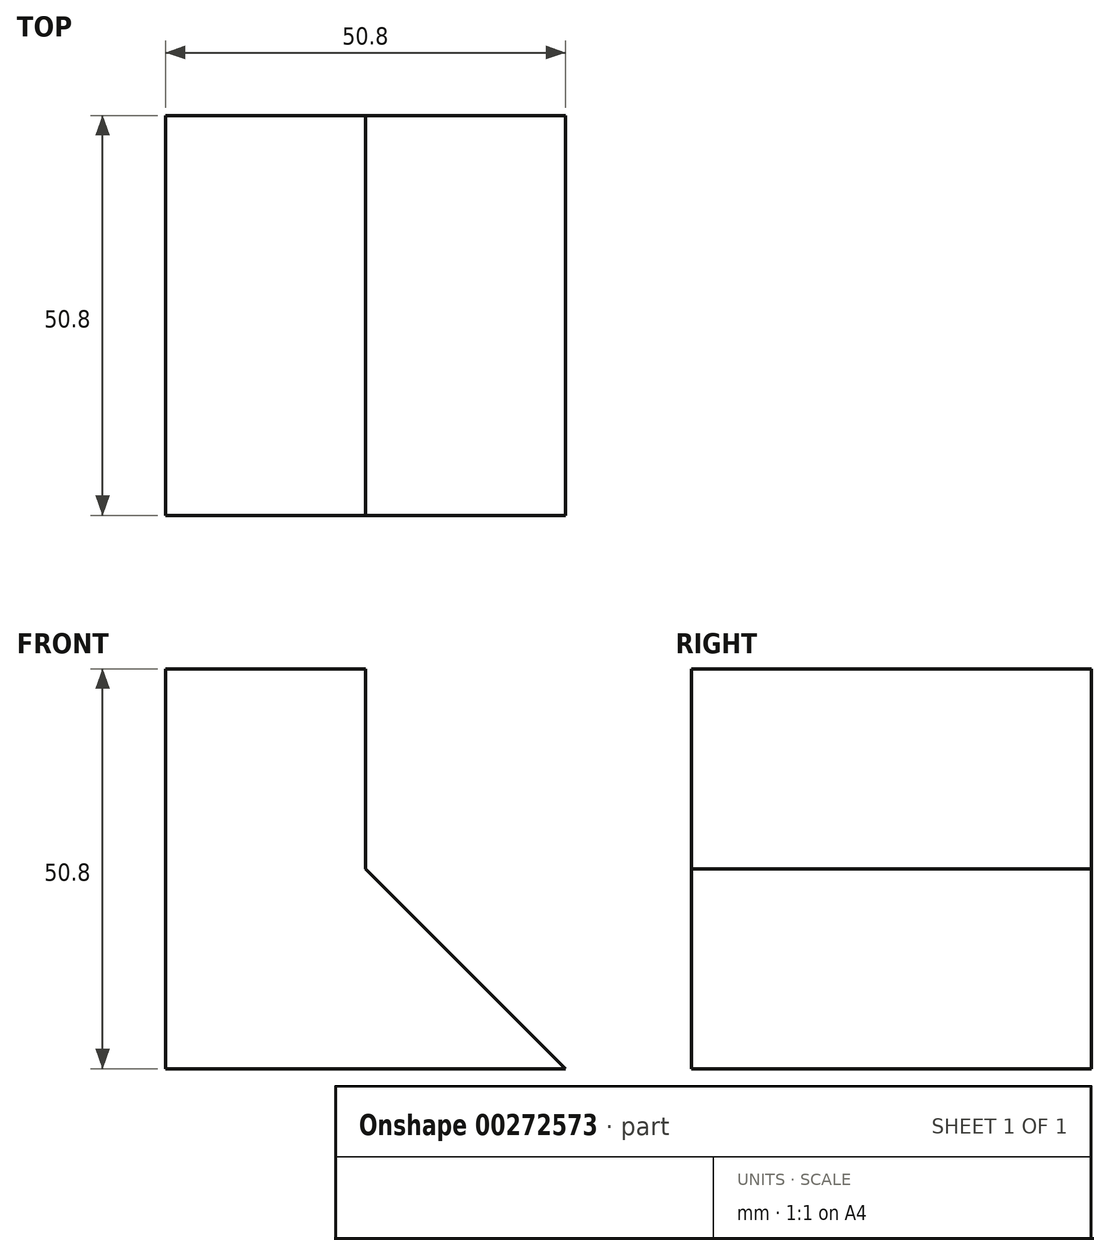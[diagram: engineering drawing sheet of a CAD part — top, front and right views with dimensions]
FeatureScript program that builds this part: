
annotation { "Feature Type Name" : "Feature", "Feature Type Description" : "" }
export const myFeature = defineFeature(function(context is Context, id is Id, definition is map)
    precondition{}
    {
        {
            var Q0;
            Q0=qCreatedBy(makeId("Front.planeOp"),FACE);
            var sketch = newSketch(context, id + "F0", { "sketchPlane" : qUnion([Q0])});
            skLineSegment(sketch, "E0", {"start": v(0, 0) * mm, "end": v(-50.8, 0) * mm});
            skLineSegment(sketch, "E1", {"start": v(-50.8, 0) * mm, "end": v(-50.8, 50.8) * mm});
            skLineSegment(sketch, "E2", {"start": v(-50.8, 50.8) * mm, "end": v(-25.4, 50.8) * mm});
            skLineSegment(sketch, "E3", {"start": v(-25.4, 50.8) * mm, "end": v(-25.4, 25.4) * mm});
            skLineSegment(sketch, "E4", {"start": v(-25.4, 25.4) * mm, "end": v(0, 0) * mm});
            skSolve(sketch);
        }
        {
            var Q0;
            Q0 = qSketchRegion(id + "F0", true);
            extrude(context, id + "F1", {"entities" : qUnion([Q0]), "depth" : 50.8 * mm});
        }
    });
